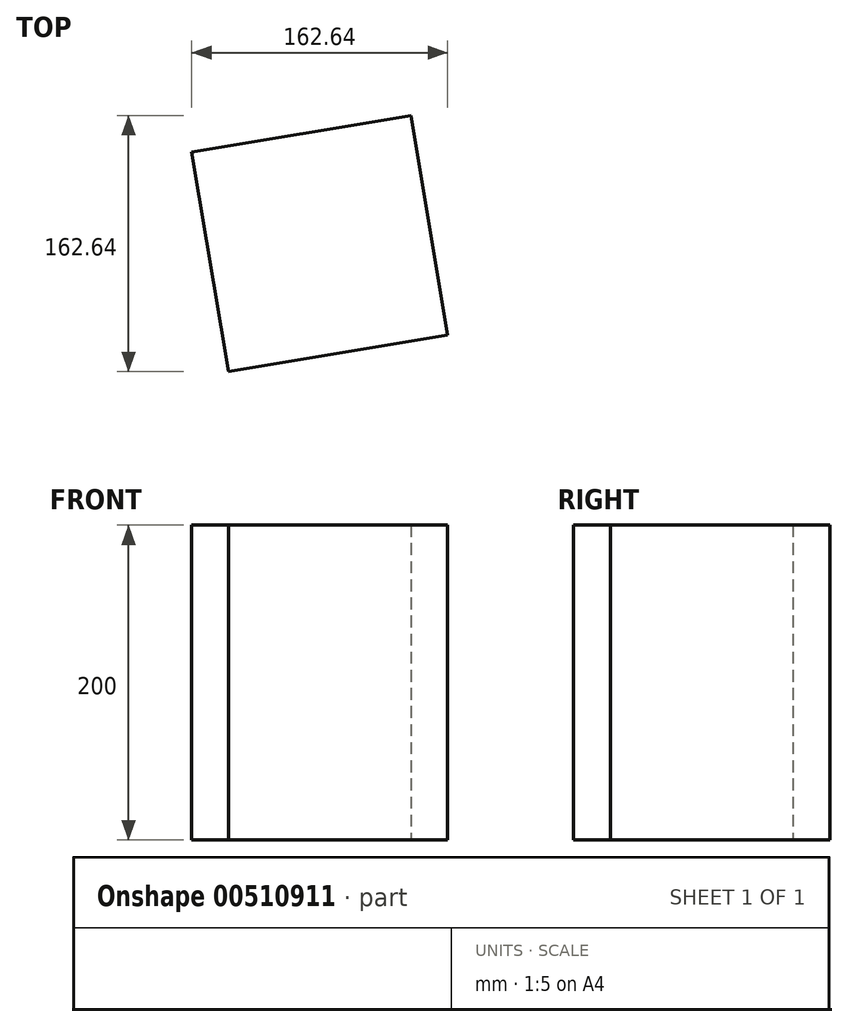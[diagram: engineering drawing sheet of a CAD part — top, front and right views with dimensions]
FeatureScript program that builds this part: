
annotation { "Feature Type Name" : "Feature", "Feature Type Description" : "" }
export const myFeature = defineFeature(function(context is Context, id is Id, definition is map)
    precondition{}
    {
        {
            var Q0;
            Q0=qCreatedBy(makeId("Top.planeOp"),FACE);
            var sketch = newSketch(context, id + "F0", { "sketchPlane" : qUnion([Q0])});
            skCircle(sketch, "E0.cCircle", {"center": v(0, 0) * mm, "radius": 99.9 * mm, "construction": true});
            skLineSegment(sketch, "E0.0", {"start": v(-58.03, -81.32) * mm, "end": v(-81.32, 58.03) * mm});
            skLineSegment(sketch, "E0.1", {"start": v(-81.32, 58.03) * mm, "end": v(58.03, 81.32) * mm});
            skLineSegment(sketch, "E0.2", {"start": v(58.03, 81.32) * mm, "end": v(81.32, -58.03) * mm});
            skLineSegment(sketch, "E0.3", {"start": v(81.32, -58.03) * mm, "end": v(-58.03, -81.32) * mm});
            skSolve(sketch);
        }
        {
            var Q0;
            Q0 = qSketchRegion(id + "F0", true);
            extrude(context, id + "F1", {"entities" : qUnion([Q0]), "depth" : 200 * mm});
        }
    });
